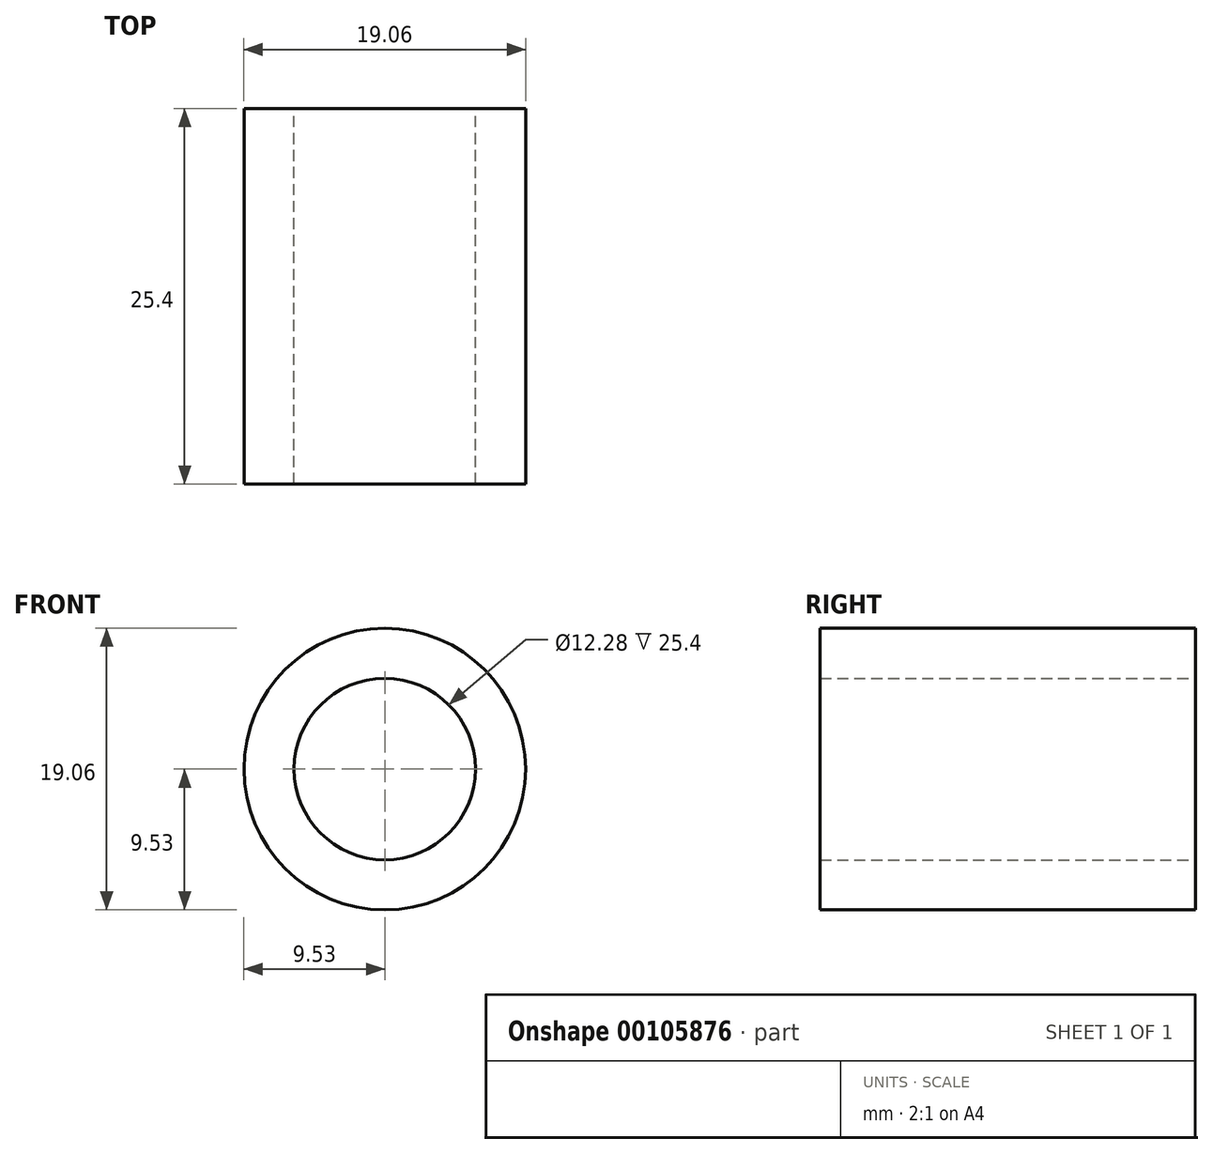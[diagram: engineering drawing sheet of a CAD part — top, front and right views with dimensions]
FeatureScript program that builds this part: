
annotation { "Feature Type Name" : "Feature", "Feature Type Description" : "" }
export const myFeature = defineFeature(function(context is Context, id is Id, definition is map)
    precondition{}
    {
        {
            var Q0;
            Q0=qCreatedBy(makeId("Front.planeOp"),FACE);
            var sketch = newSketch(context, id + "F0", { "sketchPlane" : qUnion([Q0])});
            skCircle(sketch, "E0", {"center": v(0, 0) * mm, "radius": 9.53 * mm});
            skCircle(sketch, "E1", {"center": v(0, 0) * mm, "radius": 6.14 * mm});
            skSolve(sketch);
        }
        {
            var Q0;
            Q0=makeQuery(id+"F0.imprint","IMPRINT",FACE,{"disambiguationData":[TD([[makeQuery(id+"F0.imprint","IMPRINT",EDGE,{"derivedFrom":sQuery(id+"F0.wireOp",EDGE,"E0")}),1.0]])]});
            extrude(context, id + "F1", {"entities" : qUnion([Q0]), "depth" : 25.4 * mm});
        }
    });
